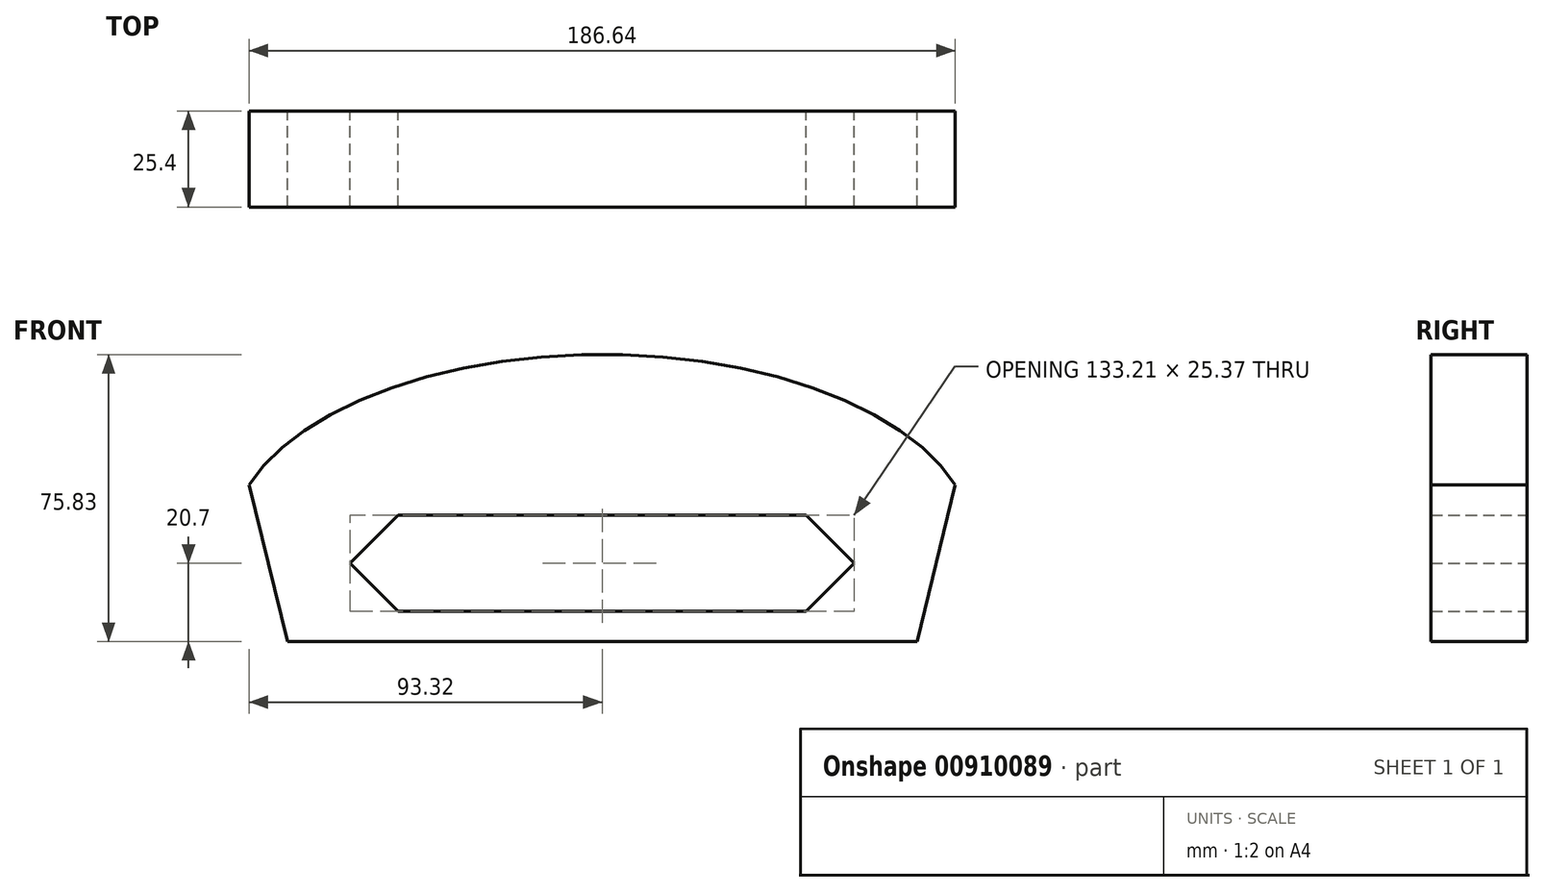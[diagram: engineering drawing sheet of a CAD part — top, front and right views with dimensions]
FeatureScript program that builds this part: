
annotation { "Feature Type Name" : "Feature", "Feature Type Description" : "" }
export const myFeature = defineFeature(function(context is Context, id is Id, definition is map)
    precondition{}
    {
        {
            var Q0;
            Q0=qCreatedBy(makeId("Front.planeOp"),FACE);
            var sketch = newSketch(context, id + "F0", { "sketchPlane" : qUnion([Q0])});
            skLineSegment(sketch, "E0", {"start": v(0, -111.68) * mm, "end": v(0, 157.97) * mm, "construction": true});
            skSolve(sketch);
        }
        {
            var Q0;
            Q0=qCreatedBy(makeId("Front.planeOp"),FACE);
            var sketch = newSketch(context, id + "F1", { "sketchPlane" : qUnion([Q0])});
            skEllipticalArc(sketch, "E1", {});
            skLineSegment(sketch, "E2", {"start": v(83.18, -92.72) * mm, "end": v(-83.18, -92.72) * mm});
            skLineSegment(sketch, "E3", {"start": v(-93.32, -51.35) * mm, "end": v(-83.18, -92.72) * mm});
            skLineSegment(sketch, "E4.MirrorCS", {"start": v(93.32, -51.35) * mm, "end": v(83.18, -92.72) * mm});
            skLineSegment(sketch, "E5.0.left", {"start": v(-53.93, -59.34) * mm, "end": v(47.83, -59.34) * mm});
            skLineSegment(sketch, "E5.0.right", {"start": v(-53.9, -84.7) * mm, "end": v(47.86, -84.7) * mm});
            skLineSegment(sketch, "E6", {"start": v(-53.9, -84.7) * mm, "end": v(-66.6, -72.04) * mm});
            skPoint(sketch, "E6.endSnap0", {"position": v(-88.25, -72.04) * mm});
            skLineSegment(sketch, "E7", {"start": v(-66.6, -72.04) * mm, "end": v(-53.93, -59.34) * mm});
            skLineSegment(sketch, "E8.MirrorCS", {"start": v(66.6, -72.04) * mm, "end": v(53.93, -59.34) * mm});
            skLineSegment(sketch, "E9.MirrorCS", {"start": v(53.9, -84.7) * mm, "end": v(66.6, -72.04) * mm});
            skLineSegment(sketch, "E10", {"start": v(53.9, -84.7) * mm, "end": v(53.9, -84.7) * mm});
            skLineSegment(sketch, "E11", {"start": v(53.9, -84.7) * mm, "end": v(47.86, -84.7) * mm});
            skLineSegment(sketch, "E12", {"start": v(47.83, -59.34) * mm, "end": v(53.93, -59.34) * mm});
            const initialGuessF1  = {"E1": [0, -0.06649376451969147, 1, 0, 0.09800392389297485, 0.04960621531707279, 0.31027530393209996, 2.8313173496576933]};
            skSetInitialGuess(sketch, initialGuessF1);
            skSolve(sketch);
        }
        {
            var Q0;
            Q0 = qSketchRegion(id + "F1", true);
            extrude(context, id + "F2", {"entities" : qUnion([Q0]), "depth" : 25.4 * mm, "offsetDistance" : 25.4 * mm});
        }
    });
